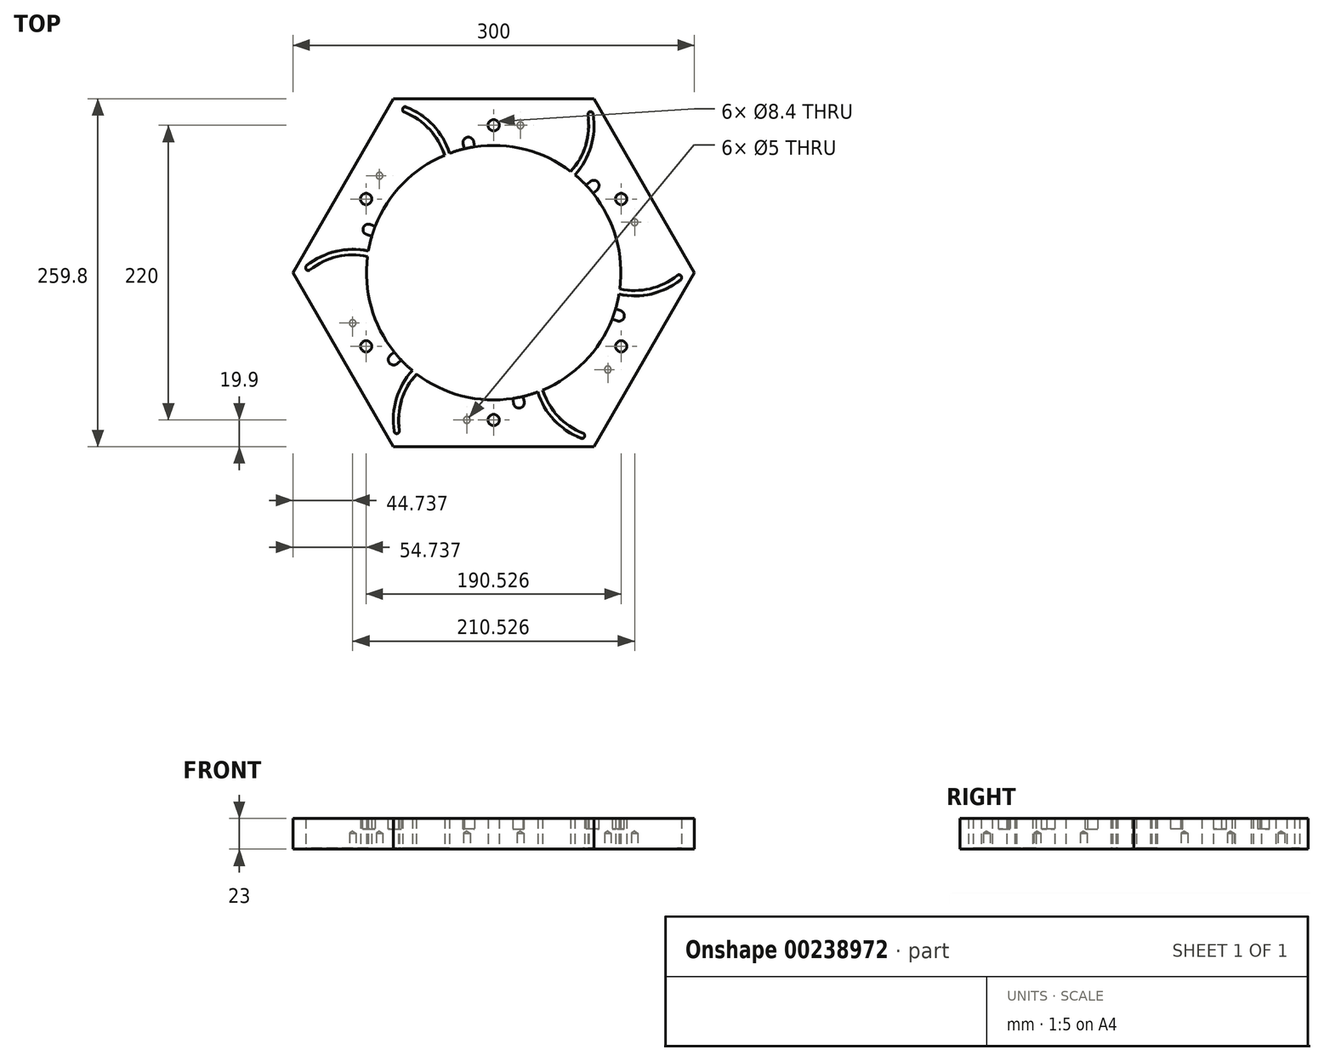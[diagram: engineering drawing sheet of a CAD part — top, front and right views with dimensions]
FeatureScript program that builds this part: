
annotation { "Feature Type Name" : "Feature", "Feature Type Description" : "" }
export const myFeature = defineFeature(function(context is Context, id is Id, definition is map)
    precondition{}
    {
        {
            var Q0;
            Q0=qCreatedBy(makeId("Top.planeOp"),FACE);
            var sketch = newSketch(context, id + "F0", { "sketchPlane" : qUnion([Q0])});
            skCircle(sketch, "E0.cCircle", {"center": v(0, 0) * mm, "radius": 150 * mm, "construction": true});
            skLineSegment(sketch, "E0.0", {"start": v(-75, 129.9) * mm, "end": v(75, 129.9) * mm});
            skLineSegment(sketch, "E0.1", {"start": v(75, 129.9) * mm, "end": v(150, 0) * mm});
            skLineSegment(sketch, "E0.2", {"start": v(150, 0) * mm, "end": v(75, -129.9) * mm});
            skLineSegment(sketch, "E0.3", {"start": v(75, -129.9) * mm, "end": v(-75, -129.9) * mm});
            skLineSegment(sketch, "E0.4", {"start": v(-75, -129.9) * mm, "end": v(-150, 0) * mm});
            skLineSegment(sketch, "E0.5", {"start": v(-150, 0) * mm, "end": v(-75, 129.9) * mm});
            skCircle(sketch, "E1", {"center": v(0, 0) * mm, "radius": 95 * mm});
            skCircle(sketch, "E2", {"center": v(0, 0) * mm, "radius": 110 * mm, "construction": true});
            skCircle(sketch, "E3", {"center": v(0, 110) * mm, "radius": 4.2 * mm});
            skCircle(sketch, "E4.1.0", {"center": v(-95.26, 55) * mm, "radius": 4.2 * mm});
            skCircle(sketch, "E4.2.0", {"center": v(-95.26, -55) * mm, "radius": 4.2 * mm});
            skCircle(sketch, "E4.3.0", {"center": v(0, -110) * mm, "radius": 4.2 * mm});
            skCircle(sketch, "E4.4.0", {"center": v(95.26, -55) * mm, "radius": 4.2 * mm});
            skCircle(sketch, "E4.5.0", {"center": v(95.26, 55) * mm, "radius": 4.2 * mm});
            skSolve(sketch);
        }
        {
            var Q0;
            Q0=qCreatedBy(makeId("Front.planeOp"),FACE);
            var sketch = newSketch(context, id + "F1", { "sketchPlane" : qUnion([Q0])});
            skLineSegment(sketch, "E5", {"start": v(0, -93.36) * mm, "end": v(0, 93) * mm, "construction": true});
            skSolve(sketch);
        }
        {
            var Q0;
            Q0=makeQuery(id+"F0.imprint","IMPRINT",FACE,{"disambiguationData":[TD([[makeQuery(id+"F0.imprint","IMPRINT",EDGE,{"derivedFrom":sQuery(id+"F0.wireOp",EDGE,"E0.0")}),-1.0]])]});
            extrude(context, id + "F2", {"entities" : qUnion([Q0]), "depth" : 25 * mm, "hasSecondDirection" : true, "secondDirectionOppositeDirection" : false, "secondDirectionDepth" : 2 * mm});
        }
        {
            var Q0;
            Q0=qCreatedBy(makeId("Top.planeOp"),FACE);
            var sketch = newSketch(context, id + "F3", { "sketchPlane" : qUnion([Q0])});
            skArc(sketch, "E6.0", {"start": v(-30.7, 79.26) * mm, "mid": v(-41.9, 106.16) * mm, "end": v(-65.27, 123.56) * mm});
            skArc(sketch, "E7.0", {"start": v(-34.54, 77.66) * mm, "mid": v(-44.72, 103.26) * mm, "end": v(-66.72, 119.83) * mm});
            skArc(sketch, "E8.0", {"start": v(-67.73, 122.7) * mm, "mid": v(-67.88, 121.03) * mm, "end": v(-66.72, 119.83) * mm});
            skArc(sketch, "E9.0", {"start": v(-65.27, 123.56) * mm, "mid": v(-66.66, 123.58) * mm, "end": v(-67.73, 122.7) * mm});
            skArc(sketch, "E10.0", {"start": v(-30.7, 79.26) * mm, "mid": v(-32.63, 78.49) * mm, "end": v(-34.54, 77.66) * mm});
            skSolve(sketch);
        }
        {
            var Q0;
            Q0=qSketchRegion(id+"F3",true);
            extrude(context, id + "F4", {"entities" : qUnion([Q0]), "depth" : 35 * mm, "hasSecondDirection" : true, "secondDirectionOppositeDirection" : true, "secondDirectionDepth" : 10 * mm});
        }
        {
            var Q0;
            Q0=makeQuery(id+"F4.opExtrude","SWEPT_BODY",BODY,{"disambiguationData":[OSD([sQuery(id+"F3.wireOp",EDGE,"E6.0"),sQuery(id+"F3.wireOp",EDGE,"E7.0"),sQuery(id+"F3.wireOp",EDGE,"E8.0"),sQuery(id+"F3.wireOp",EDGE,"E9.0"),sQuery(id+"F3.wireOp",EDGE,"E10.0")])]});
            var Q1;
            Q1=sQuery(id+"F1.wireOp",EDGE,"E5");
            circularPattern(context, id + "F5", {"entities" : qUnion([Q0]), "axis" : qUnion([Q1]), "angle" : 360 * degree, "instanceCount" : 6, "equalSpace" : true});
        }
        {
            var Q0;
            Q0=makeQuery(id+"F4.opExtrude","SWEPT_BODY",BODY,{"disambiguationData":[OSD([sQuery(id+"F3.wireOp",EDGE,"E6.0"),sQuery(id+"F3.wireOp",EDGE,"E7.0"),sQuery(id+"F3.wireOp",EDGE,"E8.0"),sQuery(id+"F3.wireOp",EDGE,"E9.0"),sQuery(id+"F3.wireOp",EDGE,"E10.0")])]});
            var Q1;
            Q1=makeQuery(id+"F5.opPattern","COPY",BODY,{"derivedFrom":makeQuery(id+"F4.opExtrude","SWEPT_BODY",BODY,{"disambiguationData":[OSD([sQuery(id+"F3.wireOp",EDGE,"E6.0"),sQuery(id+"F3.wireOp",EDGE,"E7.0"),sQuery(id+"F3.wireOp",EDGE,"E8.0"),sQuery(id+"F3.wireOp",EDGE,"E9.0"),sQuery(id+"F3.wireOp",EDGE,"E10.0")])]}),"instanceName":"5"});
            var Q2;
            Q2=makeQuery(id+"F5.opPattern","COPY",BODY,{"derivedFrom":makeQuery(id+"F4.opExtrude","SWEPT_BODY",BODY,{"disambiguationData":[OSD([sQuery(id+"F3.wireOp",EDGE,"E6.0"),sQuery(id+"F3.wireOp",EDGE,"E7.0"),sQuery(id+"F3.wireOp",EDGE,"E8.0"),sQuery(id+"F3.wireOp",EDGE,"E9.0"),sQuery(id+"F3.wireOp",EDGE,"E10.0")])]}),"instanceName":"4"});
            var Q3;
            Q3=makeQuery(id+"F5.opPattern","COPY",BODY,{"derivedFrom":makeQuery(id+"F4.opExtrude","SWEPT_BODY",BODY,{"disambiguationData":[OSD([sQuery(id+"F3.wireOp",EDGE,"E6.0"),sQuery(id+"F3.wireOp",EDGE,"E7.0"),sQuery(id+"F3.wireOp",EDGE,"E8.0"),sQuery(id+"F3.wireOp",EDGE,"E9.0"),sQuery(id+"F3.wireOp",EDGE,"E10.0")])]}),"instanceName":"3"});
            var Q4;
            Q4=makeQuery(id+"F5.opPattern","COPY",BODY,{"derivedFrom":makeQuery(id+"F4.opExtrude","SWEPT_BODY",BODY,{"disambiguationData":[OSD([sQuery(id+"F3.wireOp",EDGE,"E6.0"),sQuery(id+"F3.wireOp",EDGE,"E7.0"),sQuery(id+"F3.wireOp",EDGE,"E8.0"),sQuery(id+"F3.wireOp",EDGE,"E9.0"),sQuery(id+"F3.wireOp",EDGE,"E10.0")])]}),"instanceName":"2"});
            var Q5;
            Q5=makeQuery(id+"F5.opPattern","COPY",BODY,{"derivedFrom":makeQuery(id+"F4.opExtrude","SWEPT_BODY",BODY,{"disambiguationData":[OSD([sQuery(id+"F3.wireOp",EDGE,"E6.0"),sQuery(id+"F3.wireOp",EDGE,"E7.0"),sQuery(id+"F3.wireOp",EDGE,"E8.0"),sQuery(id+"F3.wireOp",EDGE,"E9.0"),sQuery(id+"F3.wireOp",EDGE,"E10.0")])]}),"instanceName":"1"});
            var Q6;
            Q6=makeQuery(id+"F2.opExtrude","SWEPT_BODY",BODY,{"disambiguationData":[OSD([sQuery(id+"F0.wireOp",EDGE,"E0.0"),sQuery(id+"F0.wireOp",EDGE,"E0.1"),sQuery(id+"F0.wireOp",EDGE,"E0.2"),sQuery(id+"F0.wireOp",EDGE,"E0.3"),sQuery(id+"F0.wireOp",EDGE,"E0.4"),sQuery(id+"F0.wireOp",EDGE,"E0.5"),sQuery(id+"F0.wireOp",EDGE,"E1")])]});
            booleanBodies(context, id + "F6", {"operationType" : BooleanOperationType.SUBTRACTION, "tools" : qUnion([Q0, Q1, Q2, Q3, Q4, Q5]), "targets" : qUnion([Q6])});
        }
        {
            var Q0;
            Q0=makeQuery(id+"F2.opExtrude","CAP_FACE",FACE,{"disambiguationData":[OSD([sQuery(id+"F0.wireOp",EDGE,"E0.0"),sQuery(id+"F0.wireOp",EDGE,"E0.1"),sQuery(id+"F0.wireOp",EDGE,"E0.2"),sQuery(id+"F0.wireOp",EDGE,"E0.3"),sQuery(id+"F0.wireOp",EDGE,"E0.4"),sQuery(id+"F0.wireOp",EDGE,"E0.5"),sQuery(id+"F0.wireOp",EDGE,"E1")])],"isStart":false});
            var sketch = newSketch(context, id + "F7", { "sketchPlane" : qUnion([Q0])});
            skCircle(sketch, "E11", {"center": v(0, 0) * mm, "radius": 95 * mm, "construction": true});
            skCircle(sketch, "E12", {"center": v(0, 0) * mm, "radius": 99 * mm, "construction": true});
            skLineSegment(sketch, "E13", {"start": v(0, 0) * mm, "end": v(0, 115.62) * mm, "construction": true});
            skLineSegment(sketch, "E14", {"start": v(0, 0) * mm, "end": v(-23.06, 118.63) * mm, "construction": true});
            skPoint(sketch, "E15", {"position": v(-18.9, 97.18) * mm});
            skArc(sketch, "E16", {"start": v(-19.65, 101.1) * mm, "mid": v(-22.23, 99.38) * mm, "end": v(-22.8, 96.34) * mm});
            skLineSegment(sketch, "E17", {"start": v(-22.82, 96.42) * mm, "end": v(-20.7, 85.51) * mm});
            skLineSegment(sketch, "E18", {"start": v(-16.77, 86.28) * mm, "end": v(-20.7, 85.51) * mm});
            skArc(sketch, "E19.MirrorCS", {"start": v(-19.65, 101.1) * mm, "mid": v(-16.62, 100.47) * mm, "end": v(-14.95, 97.86) * mm});
            skLineSegment(sketch, "E20.MirrorCS", {"start": v(-16.77, 86.28) * mm, "end": v(-12.84, 87.04) * mm});
            skLineSegment(sketch, "E21.MirrorCS", {"start": v(-14.96, 97.94) * mm, "end": v(-12.84, 87.04) * mm});
            skSolve(sketch);
        }
        {
            var Q0;
            Q0=qSketchRegion(id+"F7",true);
            extrude(context, id + "F8", {"entities" : qUnion([Q0]), "oppositeDirection" : true, "depth" : 8 * mm, "hasSecondDirection" : true, "secondDirectionOppositeDirection" : false, "secondDirectionDepth" : 10 * mm});
        }
        {
            var Q0;
            Q0=makeQuery(id+"F8.opExtrude","SWEPT_BODY",BODY,{"disambiguationData":[OSD([sQuery(id+"F7.wireOp",EDGE,"E16"),sQuery(id+"F7.wireOp",EDGE,"E17"),sQuery(id+"F7.wireOp",EDGE,"E18"),sQuery(id+"F7.wireOp",EDGE,"E19.MirrorCS"),sQuery(id+"F7.wireOp",EDGE,"E20.MirrorCS"),sQuery(id+"F7.wireOp",EDGE,"E21.MirrorCS")])]});
            var Q1;
            Q1=sQuery(id+"F1.wireOp",EDGE,"E5");
            circularPattern(context, id + "F9", {"operationType" : NewBodyOperationType.REMOVE, "entities" : qUnion([Q0]), "axis" : qUnion([Q1]), "angle" : 360 * degree, "instanceCount" : 6, "equalSpace" : true});
        }
        {
            var Q0;
            Q0=makeQuery(id+"F0.imprint","IMPRINT",FACE,{"disambiguationData":[TD([[makeQuery(id+"F0.imprint","IMPRINT",EDGE,{"derivedFrom":sQuery(id+"F0.wireOp",EDGE,"E0.0")}),-1.0]])]});
            cPlane(context, id + "F10", {"entities" : qUnion([Q0]), "cplaneType" : CPlaneType.OFFSET, "offset" : 0 * mm, "width" : 150 * mm, "height" : 150 * mm});
        }
        {
            var Q0;
            Q0=qCreatedBy(id+"F10.planeOp",FACE);
            var sketch = newSketch(context, id + "F11", { "sketchPlane" : qUnion([Q0])});
            skPoint(sketch, "E22.0", {"position": v(-85.26, 72.32) * mm});
            skPoint(sketch, "E23.1.0", {"position": v(-105.26, -37.68) * mm});
            skPoint(sketch, "E23.2.0", {"position": v(-20, -110) * mm});
            skPoint(sketch, "E23.3.0", {"position": v(85.26, -72.32) * mm});
            skPoint(sketch, "E23.4.0", {"position": v(105.26, 37.68) * mm});
            skPoint(sketch, "E23.5.0", {"position": v(20, 110) * mm});
            skPoint(sketch, "E23.center", {"position": v(0, 0) * mm});
            skSolve(sketch);
        }
        {
            var Q0;
            Q0=sQuery(id+"F11.wireOp",VERTEX,"E22.0");
            var Q1;
            Q1=sQuery(id+"F11.wireOp",VERTEX,"E23.5.0");
            var Q2;
            Q2=sQuery(id+"F11.wireOp",VERTEX,"E23.4.0");
            var Q3;
            Q3=sQuery(id+"F11.wireOp",VERTEX,"E23.3.0");
            var Q4;
            Q4=sQuery(id+"F11.wireOp",VERTEX,"E23.2.0");
            var Q5;
            Q5=sQuery(id+"F11.wireOp",VERTEX,"E23.1.0");
            var Q6;
            Q6=makeQuery(id+"F2.opExtrude","SWEPT_BODY",BODY,{"disambiguationData":[OSD([sQuery(id+"F0.wireOp",EDGE,"E0.0"),sQuery(id+"F0.wireOp",EDGE,"E0.1"),sQuery(id+"F0.wireOp",EDGE,"E0.2"),sQuery(id+"F0.wireOp",EDGE,"E0.3"),sQuery(id+"F0.wireOp",EDGE,"E0.4"),sQuery(id+"F0.wireOp",EDGE,"E0.5"),sQuery(id+"F0.wireOp",EDGE,"E1"),sQuery(id+"F0.wireOp",EDGE,"E3"),sQuery(id+"F0.wireOp",EDGE,"E4.1.0"),sQuery(id+"F0.wireOp",EDGE,"E4.2.0"),sQuery(id+"F0.wireOp",EDGE,"E4.3.0"),sQuery(id+"F0.wireOp",EDGE,"E4.4.0"),sQuery(id+"F0.wireOp",EDGE,"E4.5.0")])]});
            hole(context, id + "F12", {"style" : HoleStyle.SIMPLE, "endStyle" : HoleEndStyle.BLIND, "oppositeDirection" : true, "holeDiameter" : 5 * mm, "holeDepth" : 12 * mm, "locations" : qUnion([Q0, Q1, Q2, Q3, Q4, Q5]), "scope" : qUnion([Q6])});
        }
        {
            var Q0;
            Q0=makeQuery(id+"F6.opBoolean","INTERSECT",EDGE,{"derivedFrom":[makeQuery(id+"F2.opExtrude","CAP_FACE",FACE,{"disambiguationData":[OSD([sQuery(id+"F0.wireOp",EDGE,"E0.0"),sQuery(id+"F0.wireOp",EDGE,"E0.1"),sQuery(id+"F0.wireOp",EDGE,"E0.2"),sQuery(id+"F0.wireOp",EDGE,"E0.3"),sQuery(id+"F0.wireOp",EDGE,"E0.4"),sQuery(id+"F0.wireOp",EDGE,"E0.5"),sQuery(id+"F0.wireOp",EDGE,"E1"),sQuery(id+"F0.wireOp",EDGE,"E3"),sQuery(id+"F0.wireOp",EDGE,"E4.1.0"),sQuery(id+"F0.wireOp",EDGE,"E4.2.0"),sQuery(id+"F0.wireOp",EDGE,"E4.3.0"),sQuery(id+"F0.wireOp",EDGE,"E4.4.0"),sQuery(id+"F0.wireOp",EDGE,"E4.5.0")])],"isStart":true}),makeQuery(id+"F5.opPattern","COPY",FACE,{"derivedFrom":makeQuery(id+"F4.opExtrude","SWEPT_FACE",FACE,{"disambiguationData":[OSD([sQuery(id+"F3.wireOp",EDGE,"E7.0")])]}),"instanceName":"3"})]});
            var Q1;
            Q1=makeQuery(id+"F6.opBoolean","INTERSECT",EDGE,{"derivedFrom":[makeQuery(id+"F2.opExtrude","CAP_FACE",FACE,{"disambiguationData":[OSD([sQuery(id+"F0.wireOp",EDGE,"E0.0"),sQuery(id+"F0.wireOp",EDGE,"E0.1"),sQuery(id+"F0.wireOp",EDGE,"E0.2"),sQuery(id+"F0.wireOp",EDGE,"E0.3"),sQuery(id+"F0.wireOp",EDGE,"E0.4"),sQuery(id+"F0.wireOp",EDGE,"E0.5"),sQuery(id+"F0.wireOp",EDGE,"E1"),sQuery(id+"F0.wireOp",EDGE,"E3"),sQuery(id+"F0.wireOp",EDGE,"E4.1.0"),sQuery(id+"F0.wireOp",EDGE,"E4.2.0"),sQuery(id+"F0.wireOp",EDGE,"E4.3.0"),sQuery(id+"F0.wireOp",EDGE,"E4.4.0"),sQuery(id+"F0.wireOp",EDGE,"E4.5.0")])],"isStart":true}),makeQuery(id+"F5.opPattern","COPY",FACE,{"derivedFrom":makeQuery(id+"F4.opExtrude","SWEPT_FACE",FACE,{"disambiguationData":[OSD([sQuery(id+"F3.wireOp",EDGE,"E7.0")])]}),"instanceName":"4"})]});
            var Q2;
            Q2=makeQuery(id+"F6.opBoolean","INTERSECT",EDGE,{"derivedFrom":[makeQuery(id+"F2.opExtrude","CAP_FACE",FACE,{"disambiguationData":[OSD([sQuery(id+"F0.wireOp",EDGE,"E0.0"),sQuery(id+"F0.wireOp",EDGE,"E0.1"),sQuery(id+"F0.wireOp",EDGE,"E0.2"),sQuery(id+"F0.wireOp",EDGE,"E0.3"),sQuery(id+"F0.wireOp",EDGE,"E0.4"),sQuery(id+"F0.wireOp",EDGE,"E0.5"),sQuery(id+"F0.wireOp",EDGE,"E1"),sQuery(id+"F0.wireOp",EDGE,"E3"),sQuery(id+"F0.wireOp",EDGE,"E4.1.0"),sQuery(id+"F0.wireOp",EDGE,"E4.2.0"),sQuery(id+"F0.wireOp",EDGE,"E4.3.0"),sQuery(id+"F0.wireOp",EDGE,"E4.4.0"),sQuery(id+"F0.wireOp",EDGE,"E4.5.0")])],"isStart":true}),makeQuery(id+"F5.opPattern","COPY",FACE,{"derivedFrom":makeQuery(id+"F4.opExtrude","SWEPT_FACE",FACE,{"disambiguationData":[OSD([sQuery(id+"F3.wireOp",EDGE,"E7.0")])]}),"instanceName":"5"})]});
            var Q3;
            Q3=makeQuery(id+"F6.opBoolean","INTERSECT",EDGE,{"derivedFrom":[makeQuery(id+"F2.opExtrude","CAP_FACE",FACE,{"disambiguationData":[OSD([sQuery(id+"F0.wireOp",EDGE,"E0.0"),sQuery(id+"F0.wireOp",EDGE,"E0.1"),sQuery(id+"F0.wireOp",EDGE,"E0.2"),sQuery(id+"F0.wireOp",EDGE,"E0.3"),sQuery(id+"F0.wireOp",EDGE,"E0.4"),sQuery(id+"F0.wireOp",EDGE,"E0.5"),sQuery(id+"F0.wireOp",EDGE,"E1"),sQuery(id+"F0.wireOp",EDGE,"E3"),sQuery(id+"F0.wireOp",EDGE,"E4.1.0"),sQuery(id+"F0.wireOp",EDGE,"E4.2.0"),sQuery(id+"F0.wireOp",EDGE,"E4.3.0"),sQuery(id+"F0.wireOp",EDGE,"E4.4.0"),sQuery(id+"F0.wireOp",EDGE,"E4.5.0")])],"isStart":true}),makeQuery(id+"F4.opExtrude","SWEPT_FACE",FACE,{"disambiguationData":[OSD([sQuery(id+"F3.wireOp",EDGE,"E7.0")])]})]});
            var Q4;
            Q4=makeQuery(id+"F6.opBoolean","INTERSECT",EDGE,{"derivedFrom":[makeQuery(id+"F2.opExtrude","CAP_FACE",FACE,{"disambiguationData":[OSD([sQuery(id+"F0.wireOp",EDGE,"E0.0"),sQuery(id+"F0.wireOp",EDGE,"E0.1"),sQuery(id+"F0.wireOp",EDGE,"E0.2"),sQuery(id+"F0.wireOp",EDGE,"E0.3"),sQuery(id+"F0.wireOp",EDGE,"E0.4"),sQuery(id+"F0.wireOp",EDGE,"E0.5"),sQuery(id+"F0.wireOp",EDGE,"E1"),sQuery(id+"F0.wireOp",EDGE,"E3"),sQuery(id+"F0.wireOp",EDGE,"E4.1.0"),sQuery(id+"F0.wireOp",EDGE,"E4.2.0"),sQuery(id+"F0.wireOp",EDGE,"E4.3.0"),sQuery(id+"F0.wireOp",EDGE,"E4.4.0"),sQuery(id+"F0.wireOp",EDGE,"E4.5.0")])],"isStart":true}),makeQuery(id+"F5.opPattern","COPY",FACE,{"derivedFrom":makeQuery(id+"F4.opExtrude","SWEPT_FACE",FACE,{"disambiguationData":[OSD([sQuery(id+"F3.wireOp",EDGE,"E7.0")])]}),"instanceName":"1"})]});
            var Q5;
            Q5=makeQuery(id+"F6.opBoolean","INTERSECT",EDGE,{"derivedFrom":[makeQuery(id+"F2.opExtrude","CAP_FACE",FACE,{"disambiguationData":[OSD([sQuery(id+"F0.wireOp",EDGE,"E0.0"),sQuery(id+"F0.wireOp",EDGE,"E0.1"),sQuery(id+"F0.wireOp",EDGE,"E0.2"),sQuery(id+"F0.wireOp",EDGE,"E0.3"),sQuery(id+"F0.wireOp",EDGE,"E0.4"),sQuery(id+"F0.wireOp",EDGE,"E0.5"),sQuery(id+"F0.wireOp",EDGE,"E1"),sQuery(id+"F0.wireOp",EDGE,"E3"),sQuery(id+"F0.wireOp",EDGE,"E4.1.0"),sQuery(id+"F0.wireOp",EDGE,"E4.2.0"),sQuery(id+"F0.wireOp",EDGE,"E4.3.0"),sQuery(id+"F0.wireOp",EDGE,"E4.4.0"),sQuery(id+"F0.wireOp",EDGE,"E4.5.0")])],"isStart":true}),makeQuery(id+"F5.opPattern","COPY",FACE,{"derivedFrom":makeQuery(id+"F4.opExtrude","SWEPT_FACE",FACE,{"disambiguationData":[OSD([sQuery(id+"F3.wireOp",EDGE,"E7.0")])]}),"instanceName":"2"})]});
            chamfer(context, id + "F13", {"entities" : qUnion([Q0, Q1, Q2, Q3, Q4, Q5]), "width" : 0.6 * mm, "tangentPropagation" : true});
        }
        {
            var Q0;
            Q0=makeQuery(id+"F2.opExtrude","CAP_FACE",FACE,{"disambiguationData":[OSD([sQuery(id+"F0.wireOp",EDGE,"E0.0"),sQuery(id+"F0.wireOp",EDGE,"E0.1"),sQuery(id+"F0.wireOp",EDGE,"E0.2"),sQuery(id+"F0.wireOp",EDGE,"E0.3"),sQuery(id+"F0.wireOp",EDGE,"E0.4"),sQuery(id+"F0.wireOp",EDGE,"E0.5"),sQuery(id+"F0.wireOp",EDGE,"E1"),sQuery(id+"F0.wireOp",EDGE,"E3"),sQuery(id+"F0.wireOp",EDGE,"E4.1.0"),sQuery(id+"F0.wireOp",EDGE,"E4.2.0"),sQuery(id+"F0.wireOp",EDGE,"E4.3.0"),sQuery(id+"F0.wireOp",EDGE,"E4.4.0"),sQuery(id+"F0.wireOp",EDGE,"E4.5.0")])],"isStart":false});
            cPlane(context, id + "F14", {"entities" : qUnion([Q0]), "cplaneType" : CPlaneType.OFFSET, "offset" : 25 * mm, "width" : 150 * mm, "height" : 150 * mm});
        }
    });
